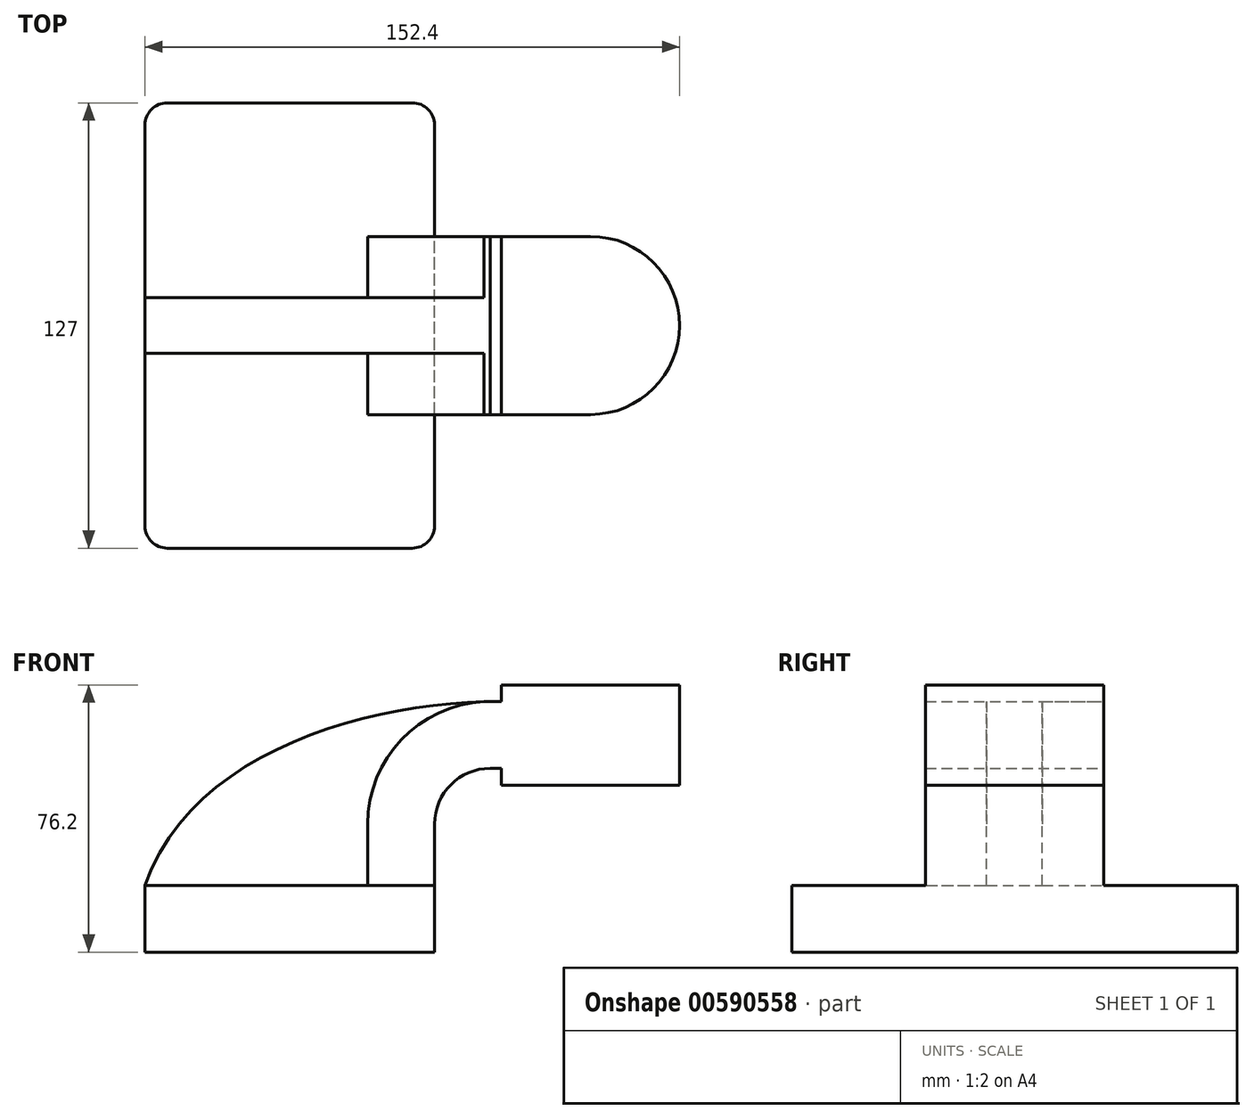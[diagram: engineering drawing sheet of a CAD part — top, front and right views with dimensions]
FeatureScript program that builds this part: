
annotation { "Feature Type Name" : "Feature", "Feature Type Description" : "" }
export const myFeature = defineFeature(function(context is Context, id is Id, definition is map)
    precondition{}
    {
        {
            var Q0;
            Q0=qCreatedBy(makeId("Front.planeOp"),FACE);
            var sketch = newSketch(context, id + "F0", { "sketchPlane" : qUnion([Q0])});
            skLineSegment(sketch, "E0.bottom", {"start": v(41.27, 9.53) * mm, "end": v(-41.27, 9.53) * mm});
            skLineSegment(sketch, "E0.top", {"start": v(41.28, -9.52) * mm, "end": v(-41.27, -9.52) * mm});
            skLineSegment(sketch, "E0.left", {"start": v(41.28, 9.53) * mm, "end": v(41.28, -9.52) * mm});
            skLineSegment(sketch, "E0.right", {"start": v(-41.27, 9.53) * mm, "end": v(-41.27, -9.52) * mm});
            skPoint(sketch, "E0.middle", {"position": v(0, 0) * mm});
            skLineSegment(sketch, "E1.bottom", {"start": v(111.12, 38.1) * mm, "end": v(60.32, 38.1) * mm});
            skLineSegment(sketch, "E1.top", {"start": v(111.12, 66.68) * mm, "end": v(60.32, 66.68) * mm});
            skLineSegment(sketch, "E1.left", {"start": v(111.12, 38.1) * mm, "end": v(111.12, 66.68) * mm});
            skLineSegment(sketch, "E1.right", {"start": v(60.32, 38.1) * mm, "end": v(60.32, 66.68) * mm});
            skPoint(sketch, "E1.middle", {"position": v(85.72, 52.39) * mm});
            skLineSegment(sketch, "E2", {"start": v(41.27, 9.53) * mm, "end": v(41.27, 27) * mm});
            skArc(sketch, "E3", {"start": v(41.27, 27) * mm, "mid": v(45.92, 38.23) * mm, "end": v(57.15, 42.88) * mm});
            skLineSegment(sketch, "E4", {"start": v(57.15, 42.88) * mm, "end": v(72.17, 42.88) * mm});
            skLineSegment(sketch, "E5.0", {"start": v(57.15, 61.93) * mm, "end": v(72.17, 61.93) * mm});
            skArc(sketch, "E5.1", {"start": v(22.23, 27) * mm, "mid": v(32.45, 51.7) * mm, "end": v(57.15, 61.93) * mm});
            skLineSegment(sketch, "E5.2", {"start": v(22.22, 9.53) * mm, "end": v(22.22, 27) * mm});
            skLineSegment(sketch, "E6", {"start": v(85.72, 38.1) * mm, "end": v(85.72, 66.68) * mm});
            skFitSpline(sketch, "E7", {"points": [v(-41.28, 9.53) * mm, v(57.15, 61.93) * mm], "startDerivative": vector(40.25, 114.47) * mm, "endDerivative": vector(107.58, 2.09) * mm});
            skSolve(sketch);
        }
        {
            var Q0;
            Q0=makeQuery(id+"F0.imprint","IMPRINT",FACE,{"disambiguationData":[TD([[makeQuery(id+"F0.imprint","IMPRINT",EDGE,{"derivedFrom":sQuery(id+"F0.wireOp",EDGE,"E0.top")}),-1.0]])]});
            extrude(context, id + "F1", {"entities" : qUnion([Q0]), "endBound" : BoundingType.SYMMETRIC, "depth" : 127 * mm, "offsetDistance" : 25.4 * mm});
        }
        {
            var Q0;
            {var subQ1=sQuery(id+"F0.wireOp",EDGE,"E2");Q0=makeQuery(id+"F0.imprint","IMPRINT",FACE,{"disambiguationData":[TD([[makeQuery(id+"F0.imprint","IMPRINT",EDGE,{"derivedFrom":subQ1}),1.0]])]});}
            var Q1;
            {var subQ6=sQuery(id+"F0.wireOp",EDGE,"E6");Q1=makeQuery(id+"F0.imprint","IMPRINT",FACE,{"disambiguationData":[TD([[makeQuery(id+"F0.imprint","IMPRINT",EDGE,{"derivedFrom":subQ6}),1.0]])]});}
            extrude(context, id + "F2", {"entities" : qUnion([Q0, Q1]), "operationType" : NewBodyOperationType.ADD, "endBound" : BoundingType.SYMMETRIC, "depth" : 50.8 * mm, "offsetDistance" : 25.4 * mm});
        }
        {
            var Q0;
            {var subQ3=sQuery(id+"F0.wireOp",EDGE,"E5.2");Q0=makeQuery(id+"F0.imprint","IMPRINT",FACE,{"disambiguationData":[TD([[makeQuery(id+"F0.imprint","IMPRINT",EDGE,{"derivedFrom":subQ3}),1.0]])]});}
            extrude(context, id + "F3", {"entities" : qUnion([Q0]), "operationType" : NewBodyOperationType.ADD, "endBound" : BoundingType.SYMMETRIC, "depth" : 15.88 * mm, "offsetDistance" : 25.4 * mm});
        }
        {
            var Q0;
            {var subQ0=sQuery(id+"F0.wireOp",EDGE,"E1.left");Q0=makeQuery(id+"F0.imprint","IMPRINT",FACE,{"disambiguationData":[TD([[makeQuery(id+"F0.imprint","IMPRINT",EDGE,{"derivedFrom":subQ0}),1.0]])]});}
            var Q1;
            Q1=sQuery(id+"F0.wireOp",EDGE,"E6");
            revolve(context, id + "F4", {"operationType" : NewBodyOperationType.ADD, "entities" : qUnion([Q0]), "axis" : qUnion([Q1]), "revolveType" : RevolveType.FULL});
        }
        {
            var Q0;
            Q0=makeQuery(id+"F1.opExtrude","CAP_EDGE",EDGE,{"disambiguationData":[OSD([sQuery(id+"F0.wireOp",EDGE,"E0.right")])],"isStart":false});
            var Q1;
            Q1=makeQuery(id+"F1.opExtrude","CAP_EDGE",EDGE,{"disambiguationData":[OSD([sQuery(id+"F0.wireOp",EDGE,"E0.left")])],"isStart":false});
            var Q2;
            Q2=makeQuery(id+"F1.opExtrude","CAP_EDGE",EDGE,{"disambiguationData":[OSD([sQuery(id+"F0.wireOp",EDGE,"E0.left")])],"isStart":true});
            var Q3;
            Q3=makeQuery(id+"F1.opExtrude","CAP_EDGE",EDGE,{"disambiguationData":[OSD([sQuery(id+"F0.wireOp",EDGE,"E0.right")])],"isStart":true});
            fillet(context, id + "F5", {"entities" : qUnion([Q0, Q1, Q2, Q3]), "radius" : 6.35 * mm, "tangentPropagation" : true, "allowEdgeOverflow" : false});
        }
    });
